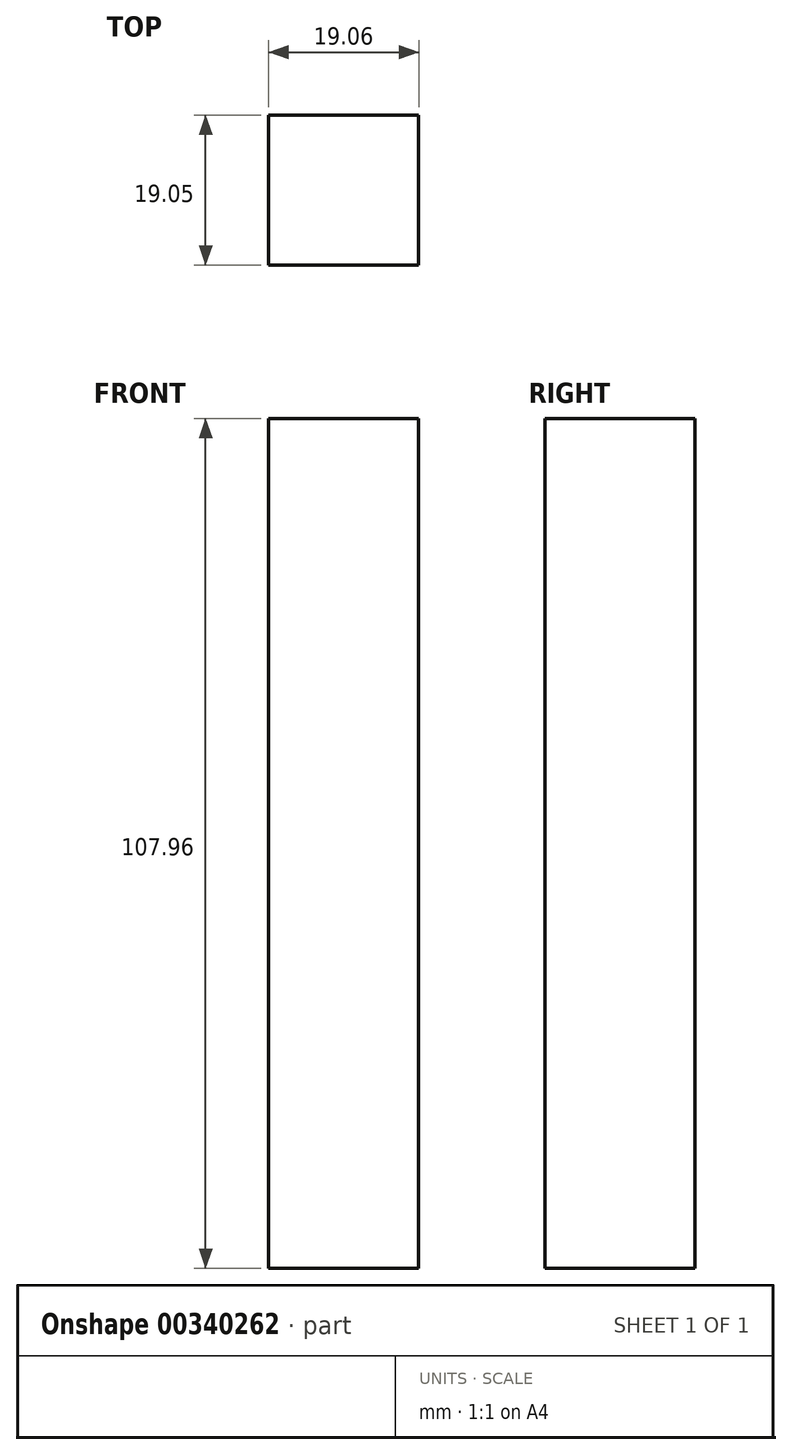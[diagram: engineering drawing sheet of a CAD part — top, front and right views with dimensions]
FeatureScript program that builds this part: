
annotation { "Feature Type Name" : "Feature", "Feature Type Description" : "" }
export const myFeature = defineFeature(function(context is Context, id is Id, definition is map)
    precondition{}
    {
        {
            var Q0;
            Q0=qCreatedBy(makeId("Front.planeOp"),FACE);
            var sketch = newSketch(context, id + "F0", { "sketchPlane" : qUnion([Q0])});
            skLineSegment(sketch, "E0.bottom", {"start": v(9.52, -53.98) * mm, "end": v(-9.53, -53.98) * mm});
            skLineSegment(sketch, "E0.top", {"start": v(9.53, 53.97) * mm, "end": v(-9.52, 53.97) * mm});
            skLineSegment(sketch, "E0.left", {"start": v(9.52, -53.98) * mm, "end": v(9.53, 53.97) * mm});
            skLineSegment(sketch, "E0.right", {"start": v(-9.53, -53.98) * mm, "end": v(-9.52, 53.97) * mm});
            skPoint(sketch, "E0.middle", {"position": v(0, 0) * mm});
            skSolve(sketch);
        }
        {
            var Q0;
            Q0 = qSketchRegion(id + "F0", true);
            extrude(context, id + "F1", {"entities" : qUnion([Q0]), "depth" : 19.05 * mm});
        }
    });
